# Revit family: TapSet_Basin_Nero_Mecca_Arc_Spout
name_source: partatom
category: Plumbing Fixtures
units: mm (PartAtom-declared; Revit-internal decimal feet)

## family parameters
Always vertical = Yes
Cut with Voids When Loaded = Yes
Maintain Annotation Orientation = No
OmniClass Number = 23.31.11.19
OmniClass Title = Faucet Mixing Valves
Part Type = Normal
Room Calculation Point = No
Round Connector Dimension = Use Diameter
Shared = No
Work Plane-Based = No

## types (7) — shared parameters
Assembly Code = D2010
CW Connection = Yes
Default Elevation = 900 mm
HW Connection = Yes
IfcExportAs = IfcValve
IfcExportType = MIXING
Manufacturer = Nero
ManufacturerOverallDepth = 175 mm  [stored 0.574147 ft]
ManufacturerOverallHeight = 210 mm  [stored 0.688976 ft]
ManufacturerOverallWidth = 396 mm  [stored 1.29921 ft]
ModifiedIssue = 20251009 $
URL = https://nerotapware.com.au
Uniclass2015Code = Pr_40_20_87
Uniclass2015Title = Taps and water supply outlet fittings
Uniclass2015Version = Products v1.35
Vent Connection = No
Waste Connection = No
zero-valued in all types: CWFU, HWFU, WFU

## per-type parameters (varying)
| type | Description | ManufacturerSpecCode | Material | Model | Type Comments |
| Chrome (25D002CH) | Mecca Basin Set Arc Spout Chrome | 25D002CH | Metal_Chrome_Nero | 25D002CH | Tap Set - Basin - Arc - Spout - Chrome |
| Matte Black (25D002MB) | Mecca Basin Set Arc Spout Matte Black | 25D002MB | Metal_MatteBlack_Nero | 25D002MB | Tap Set - Basin - Arc - Spout - Matte Black |
| Brushed Nickel (25D002BN) | Mecca Basin Set Arc Spout Brushed Nickel | 25D002BN | Metal_Nickel_Nero_Brushed | 25D002BN | Tap Set - Basin - Arc - Spout - Brushed Nickel |
| Gun Metal (25D002GM) | Mecca Basin Set Arc Spout Gun Metal | 25D002GM | Metal_GunMetal_Nero | 25D002GM | Tap Set - Basin - Arc - Spout - Gun Metal |
| Brushed Gold (25D002BG) | Mecca Basin Set Arc Spout Brushed Gold | 25D002BG | Metal_Gold_Nero_Brushed | 25D002BG | Tap Set - Basin - Arc - Spout - Brushed Gold |
| Brushed Bronze (25D002BZ) | Mecca Basin Set Arc Spout Brushed Bronze | 25D002BZ | Metal_Bronze_Nero_Brushed | 25D002BZ | Tap Set - Basin - Arc - Spout - Brushed Bronze |
| Matte White (25D002MW) | Mecca Basin Set Arc Spout Matte White | 25D002MW | Metal_MatteWhite_Nero | 25D002MW | Tap Set - Basin - Arc - Spout - Matte White |

note: [stored X ft] marks values corroborated as IEEE doubles in the binary element streams (Revit-internal decimal feet)

## geometry (parser evidence)
native form markers: Sweep x2
no freeform markers — native parametric forms only
